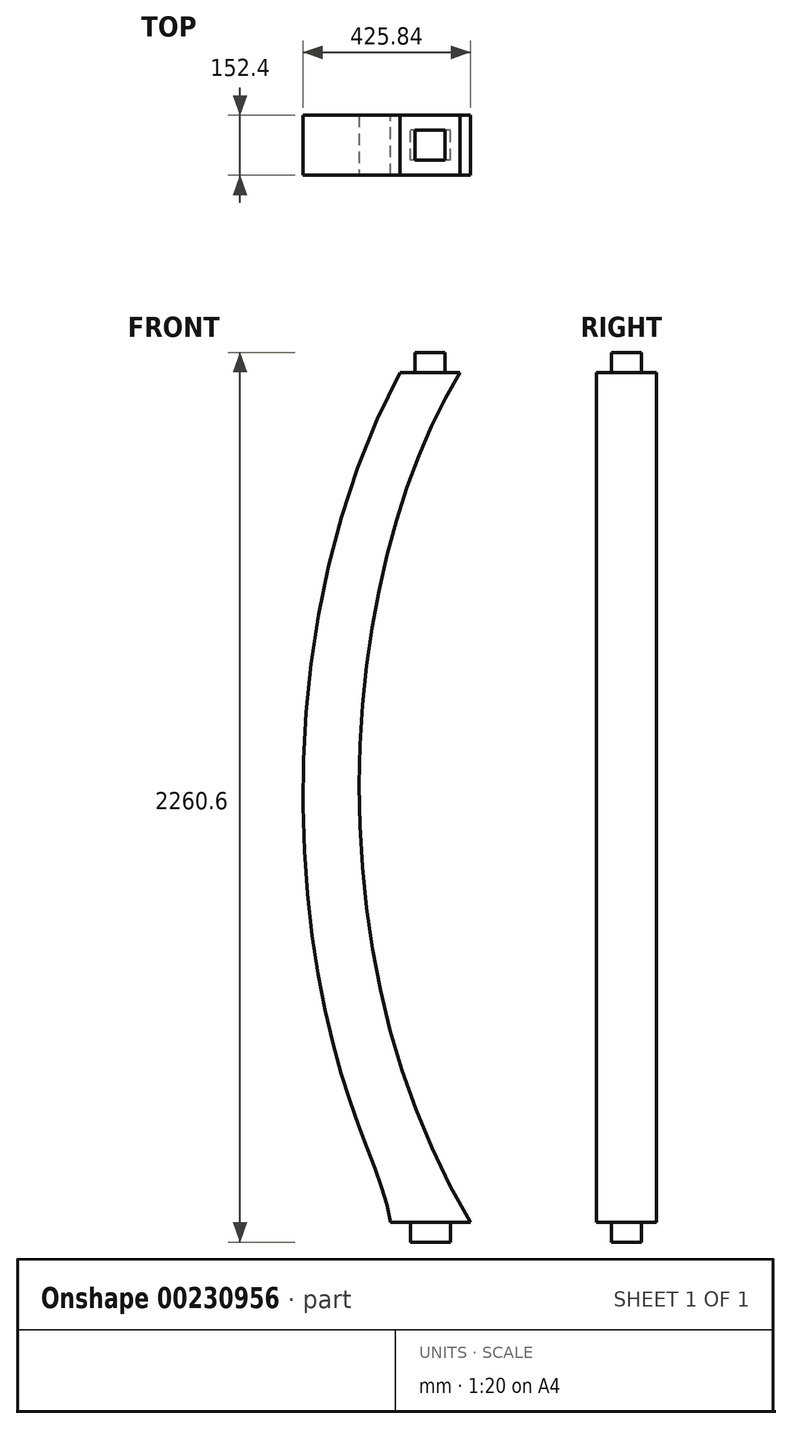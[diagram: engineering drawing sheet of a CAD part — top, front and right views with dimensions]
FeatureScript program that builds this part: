
annotation { "Feature Type Name" : "Feature", "Feature Type Description" : "" }
export const myFeature = defineFeature(function(context is Context, id is Id, definition is map)
    precondition{}
    {
        {
            var Q0;
            Q0=qCreatedBy(makeId("Front.planeOp"),FACE);
            var sketch = newSketch(context, id + "F0", { "sketchPlane" : qUnion([Q0])});
            skLineSegment(sketch, "E0", {"start": v(0, -1193.8) * mm, "end": v(-919.23, -1193.8) * mm});
            skLineSegment(sketch, "E1", {"start": v(0, 965.2) * mm, "end": v(-945.58, 965.2) * mm});
            skFitSpline(sketch, "E2", {"points": [v(-945.58, 965.2) * mm, v(-919.23, -1193.8) * mm], "startDerivative": vector(-889.45, -1441.33) * mm, "endDerivative": vector(1263.87, -2098.17) * mm});
            skLineSegment(sketch, "E3", {"start": v(-945.58, 965.2) * mm, "end": v(-1097.98, 965.2) * mm});
            skLineSegment(sketch, "E4", {"start": v(-919.23, -1193.8) * mm, "end": v(-1122.43, -1193.8) * mm});
            skFitSpline(sketch, "E5", {"points": [v(-1097.98, 965.2) * mm, v(-1266.7, -749.28) * mm, v(-1122.43, -1193.8) * mm], "startDerivative": vector(-1456.54, -2733.7) * mm, "endDerivative": vector(159.23, -982.95) * mm});
            skSolve(sketch);
        }
        {
            var Q0;
            Q0=qSketchRegion(id+"F0",true);
            extrude(context, id + "F1", {"entities" : qUnion([Q0]), "endBound" : BoundingType.SYMMETRIC, "depth" : 152.4 * mm});
        }
        {
            var Q0;
            Q0=makeQuery(id+"F1.opExtrude","SWEPT_FACE",FACE,{"disambiguationData":[OSD([sQuery(id+"F0.wireOp",EDGE,"E4")])]});
            var sketch = newSketch(context, id + "F2", { "sketchPlane" : qUnion([Q0])});
            skLineSegment(sketch, "E6.bottom", {"start": v(-970.03, 38.1) * mm, "end": v(-1071.63, 38.1) * mm});
            skLineSegment(sketch, "E6.top", {"start": v(-970.03, -38.1) * mm, "end": v(-1071.63, -38.1) * mm});
            skLineSegment(sketch, "E6.left", {"start": v(-970.03, 38.1) * mm, "end": v(-970.03, -38.1) * mm});
            skLineSegment(sketch, "E6.right", {"start": v(-1071.63, 38.1) * mm, "end": v(-1071.63, -38.1) * mm});
            skPoint(sketch, "E6.middle", {"position": v(-1020.83, 0) * mm});
            skSolve(sketch);
        }
        {
            var Q0;
            Q0=qSketchRegion(id+"F2",true);
            extrude(context, id + "F3", {"entities" : qUnion([Q0]), "operationType" : NewBodyOperationType.ADD, "depth" : 50.8 * mm});
        }
        {
            var Q0;
            Q0=makeQuery(id+"F1.opExtrude","SWEPT_FACE",FACE,{"disambiguationData":[OSD([sQuery(id+"F0.wireOp",EDGE,"E3")])]});
            var sketch = newSketch(context, id + "F4", { "sketchPlane" : qUnion([Q0])});
            skLineSegment(sketch, "E7.bottom", {"start": v(-983.68, 38.1) * mm, "end": v(-1059.88, 38.1) * mm});
            skLineSegment(sketch, "E7.top", {"start": v(-983.68, -38.1) * mm, "end": v(-1059.88, -38.1) * mm});
            skLineSegment(sketch, "E7.left", {"start": v(-983.68, 38.1) * mm, "end": v(-983.68, -38.1) * mm});
            skLineSegment(sketch, "E7.right", {"start": v(-1059.88, 38.1) * mm, "end": v(-1059.88, -38.1) * mm});
            skPoint(sketch, "E7.middle", {"position": v(-1021.78, 0) * mm});
            skSolve(sketch);
        }
        {
            var Q0;
            Q0=qSketchRegion(id+"F4",true);
            extrude(context, id + "F5", {"entities" : qUnion([Q0]), "operationType" : NewBodyOperationType.ADD, "depth" : 50.8 * mm});
        }
    });
